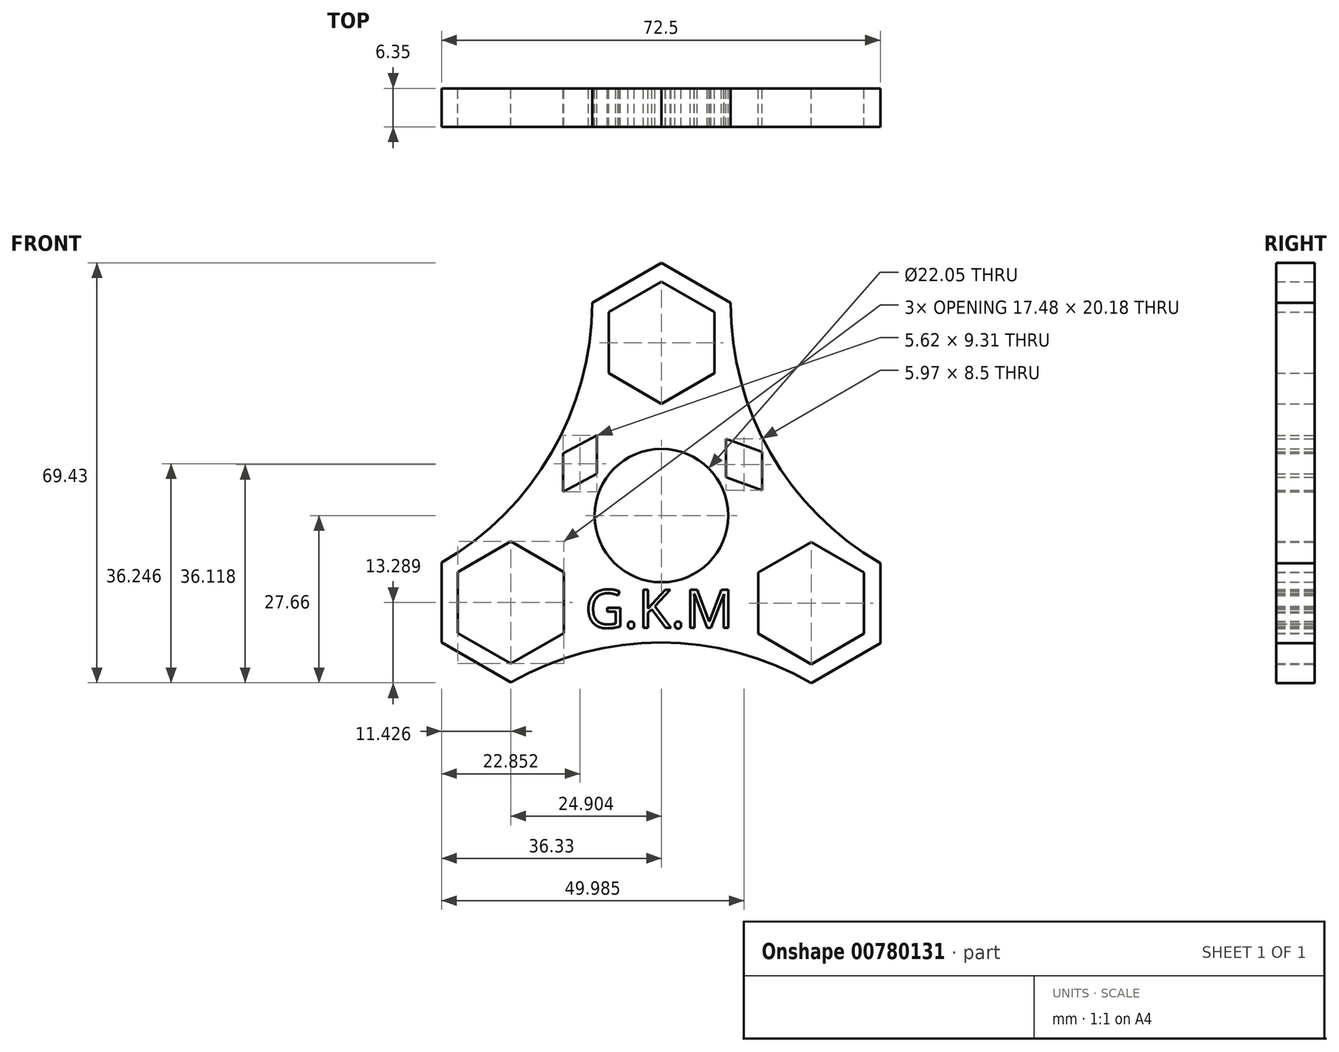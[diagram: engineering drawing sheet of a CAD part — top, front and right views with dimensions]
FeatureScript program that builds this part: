
annotation { "Feature Type Name" : "Feature", "Feature Type Description" : "" }
export const myFeature = defineFeature(function(context is Context, id is Id, definition is map)
    precondition{}
    {
        {
            var Q0;
            Q0=qCreatedBy(makeId("Front.planeOp"),FACE);
            var sketch = newSketch(context, id + "F0", { "sketchPlane" : qUnion([Q0])});
            skCircle(sketch, "E0", {"center": v(0, 0) * mm, "radius": 11.02 * mm});
            skCircle(sketch, "E1.cCircle", {"center": v(0, 28.58) * mm, "radius": 8.74 * mm, "construction": true});
            skLineSegment(sketch, "E1.0", {"start": v(-8.74, 23.53) * mm, "end": v(-8.74, 33.62) * mm});
            skLineSegment(sketch, "E1.1", {"start": v(-8.74, 33.62) * mm, "end": v(0, 38.66) * mm});
            skLineSegment(sketch, "E1.2", {"start": v(0, 38.66) * mm, "end": v(8.74, 33.62) * mm});
            skLineSegment(sketch, "E1.3", {"start": v(8.74, 33.62) * mm, "end": v(8.74, 23.53) * mm});
            skLineSegment(sketch, "E1.4", {"start": v(8.74, 23.53) * mm, "end": v(0, 18.49) * mm});
            skLineSegment(sketch, "E1.5", {"start": v(0, 18.49) * mm, "end": v(-8.74, 23.53) * mm});
            skPoint(sketch, "E1.0.midPoint", {"position": v(-8.74, 28.58) * mm});
            skCircle(sketch, "E2.cCircle", {"center": v(0, 28.58) * mm, "radius": 11.43 * mm, "construction": true});
            skLineSegment(sketch, "E2.0", {"start": v(-11.43, 21.98) * mm, "end": v(-11.43, 35.17) * mm});
            skLineSegment(sketch, "E2.1", {"start": v(-11.43, 35.17) * mm, "end": v(0, 41.77) * mm});
            skLineSegment(sketch, "E2.2", {"start": v(0, 41.77) * mm, "end": v(11.43, 35.17) * mm});
            skLineSegment(sketch, "E2.3", {"start": v(11.43, 35.17) * mm, "end": v(11.43, 21.98) * mm});
            skLineSegment(sketch, "E2.4", {"start": v(11.43, 21.98) * mm, "end": v(0, 15.38) * mm});
            skLineSegment(sketch, "E2.5", {"start": v(0, 15.38) * mm, "end": v(-11.43, 21.98) * mm});
            skPoint(sketch, "E2.0.midPoint", {"position": v(-11.43, 28.57) * mm});
            skLineSegment(sketch, "E3.1.0", {"start": v(-24.9, -27.57) * mm, "end": v(-36.33, -20.97) * mm});
            skLineSegment(sketch, "E3.1.1", {"start": v(-36.33, -20.97) * mm, "end": v(-36.33, -7.77) * mm});
            skPoint(sketch, "E3.1.2", {"position": v(-20.54, -21.94) * mm});
            skLineSegment(sketch, "E3.1.3", {"start": v(-24.9, -24.46) * mm, "end": v(-33.64, -19.42) * mm});
            skCircle(sketch, "E3.1.4", {"center": v(-24.9, -14.37) * mm, "radius": 8.74 * mm, "construction": true});
            skPoint(sketch, "E3.1.5", {"position": v(-19.19, -24.27) * mm});
            skLineSegment(sketch, "E3.1.6", {"start": v(-13.47, -7.77) * mm, "end": v(-13.47, -20.97) * mm});
            skLineSegment(sketch, "E3.1.7", {"start": v(-24.9, -1.17) * mm, "end": v(-13.47, -7.77) * mm});
            skLineSegment(sketch, "E3.1.8", {"start": v(-36.33, -7.77) * mm, "end": v(-24.9, -1.17) * mm});
            skLineSegment(sketch, "E3.1.9", {"start": v(-13.47, -20.97) * mm, "end": v(-24.9, -27.57) * mm});
            skCircle(sketch, "E3.1.10", {"center": v(-24.9, -14.37) * mm, "radius": 11.43 * mm, "construction": true});
            skLineSegment(sketch, "E3.1.11", {"start": v(-24.9, -4.28) * mm, "end": v(-16.17, -9.33) * mm});
            skLineSegment(sketch, "E3.1.12", {"start": v(-16.17, -9.33) * mm, "end": v(-16.17, -19.42) * mm});
            skLineSegment(sketch, "E3.1.13", {"start": v(-16.17, -19.42) * mm, "end": v(-24.9, -24.46) * mm});
            skLineSegment(sketch, "E3.1.14", {"start": v(-33.64, -19.42) * mm, "end": v(-33.64, -9.33) * mm});
            skLineSegment(sketch, "E3.1.15", {"start": v(-33.64, -9.33) * mm, "end": v(-24.9, -4.28) * mm});
            skLineSegment(sketch, "E3.2.0", {"start": v(36.17, -7.87) * mm, "end": v(36.17, -21.07) * mm});
            skLineSegment(sketch, "E3.2.1", {"start": v(36.17, -21.07) * mm, "end": v(24.74, -27.66) * mm});
            skPoint(sketch, "E3.2.2", {"position": v(29.1, -6.9) * mm});
            skLineSegment(sketch, "E3.2.3", {"start": v(33.48, -9.42) * mm, "end": v(33.48, -19.51) * mm});
            skCircle(sketch, "E3.2.4", {"center": v(24.74, -14.47) * mm, "radius": 8.74 * mm, "construction": true});
            skPoint(sketch, "E3.2.5", {"position": v(30.46, -4.57) * mm});
            skLineSegment(sketch, "E3.2.6", {"start": v(13.31, -7.87) * mm, "end": v(24.74, -1.27) * mm});
            skLineSegment(sketch, "E3.2.7", {"start": v(13.31, -21.07) * mm, "end": v(13.31, -7.87) * mm});
            skLineSegment(sketch, "E3.2.8", {"start": v(24.74, -27.66) * mm, "end": v(13.31, -21.07) * mm});
            skLineSegment(sketch, "E3.2.9", {"start": v(24.74, -1.27) * mm, "end": v(36.17, -7.87) * mm});
            skCircle(sketch, "E3.2.10", {"center": v(24.74, -14.47) * mm, "radius": 11.43 * mm, "construction": true});
            skLineSegment(sketch, "E3.2.11", {"start": v(16, -19.51) * mm, "end": v(16, -9.42) * mm});
            skLineSegment(sketch, "E3.2.12", {"start": v(16, -9.42) * mm, "end": v(24.74, -4.38) * mm});
            skLineSegment(sketch, "E3.2.13", {"start": v(24.74, -4.38) * mm, "end": v(33.48, -9.42) * mm});
            skLineSegment(sketch, "E3.2.14", {"start": v(33.48, -19.51) * mm, "end": v(24.74, -24.56) * mm});
            skLineSegment(sketch, "E3.2.15", {"start": v(24.74, -24.56) * mm, "end": v(16, -19.51) * mm});
            skCircle(sketch, "E3.2.16", {"center": v(0, -0.18) * mm, "radius": 14.29 * mm});
            skPoint(sketch, "E3.center", {"position": v(-0.05, -0.09) * mm});
            skArc(sketch, "E4", {"start": v(11.43, 35.17) * mm, "mid": v(18.01, 10.33) * mm, "end": v(36.17, -7.87) * mm});
            skArc(sketch, "E5", {"start": v(-36.33, -7.77) * mm, "mid": v(-18.15, 10.38) * mm, "end": v(-11.43, 35.17) * mm});
            skArc(sketch, "E6", {"start": v(24.74, -27.66) * mm, "mid": v(-0.07, -21) * mm, "end": v(-24.9, -27.57) * mm});
            skSolve(sketch);
        }
        {
            var Q0;
            Q0=makeQuery(id+"F0.imprint","IMPRINT",FACE,{"disambiguationData":[TD([[makeQuery(id+"F0.imprint","IMPRINT",EDGE,{"derivedFrom":sQuery(id+"F0.wireOp",EDGE,"E0")}),-1.0]])]});
            var Q1;
            Q1=makeQuery(id+"F0.imprint","IMPRINT",FACE,{"disambiguationData":[TD([[makeQuery(id+"F0.imprint","IMPRINT",EDGE,{"derivedFrom":sQuery(id+"F0.wireOp",EDGE,"E1.0")}),1.0]])]});
            var Q2;
            Q2=makeQuery(id+"F0.imprint","IMPRINT",FACE,{"disambiguationData":[TD([[makeQuery(id+"F0.imprint","IMPRINT",EDGE,{"derivedFrom":sQuery(id+"F0.wireOp",EDGE,"E2.0")}),1.0]])]});
            var Q3;
            Q3=makeQuery(id+"F0.imprint","IMPRINT",FACE,{"disambiguationData":[TD([[makeQuery(id+"F0.imprint","IMPRINT",EDGE,{"derivedFrom":sQuery(id+"F0.wireOp",EDGE,"E3.1.0")}),-1.0]])]});
            var Q4;
            Q4=makeQuery(id+"F0.imprint","IMPRINT",FACE,{"disambiguationData":[TD([[makeQuery(id+"F0.imprint","IMPRINT",EDGE,{"derivedFrom":sQuery(id+"F0.wireOp",EDGE,"E3.2.0")}),-1.0]])]});
            extrude(context, id + "F1", {"entities" : qUnion([Q0, Q1, Q2, Q3, Q4]), "depth" : 6.35 * mm, "offsetDistance" : 25.4 * mm});
        }
        {
            var Q0;
            Q0=qCreatedBy(makeId("Front.planeOp"),FACE);
            var sketch = newSketch(context, id + "F2", { "sketchPlane" : qUnion([Q0])});
            skText(sketch, "E7", { "text": "G.K.M", "fontName": "OpenSans-Regular.ttf"});
            const initialGuessF2  = {"E7": [-0.01261, -0.01856, 1, 0, 0.00635]};
            skSetInitialGuess(sketch, initialGuessF2);
            skSolve(sketch);
        }
        {
            var Q0;
            Q0 = qSketchRegion(id + "F2", true);
            extrude(context, id + "F3", {"entities" : qUnion([Q0]), "operationType" : NewBodyOperationType.REMOVE, "depth" : 25.4 * mm, "offsetDistance" : 25.4 * mm});
        }
        {
            var Q0;
            Q0=qCreatedBy(makeId("Front.planeOp"),FACE);
            var sketch = newSketch(context, id + "F4", { "sketchPlane" : qUnion([Q0])});
            skLineSegment(sketch, "E8", {"start": v(-10.67, 13.24) * mm, "end": v(-16.29, 10.28) * mm});
            skLineSegment(sketch, "E9", {"start": v(-10.67, 13.24) * mm, "end": v(-10.67, 6.89) * mm});
            skLineSegment(sketch, "E10", {"start": v(-16.29, 10.28) * mm, "end": v(-16.29, 3.93) * mm});
            skLineSegment(sketch, "E11", {"start": v(-10.67, 6.89) * mm, "end": v(-16.29, 3.93) * mm});
            skLineSegment(sketch, "E12", {"start": v(10.67, 12.7) * mm, "end": v(10.67, 6.36) * mm});
            skLineSegment(sketch, "E13", {"start": v(10.67, 12.7) * mm, "end": v(16.64, 10.56) * mm});
            skLineSegment(sketch, "E14", {"start": v(16.64, 10.56) * mm, "end": v(16.64, 4.2) * mm});
            skLineSegment(sketch, "E15", {"start": v(10.67, 6.36) * mm, "end": v(16.64, 4.2) * mm});
            skSolve(sketch);
        }
        {
            var Q0;
            Q0 = qSketchRegion(id + "F4", true);
            extrude(context, id + "F5", {"entities" : qUnion([Q0]), "operationType" : NewBodyOperationType.REMOVE, "depth" : 25.4 * mm, "offsetDistance" : 25.4 * mm});
        }
    });
